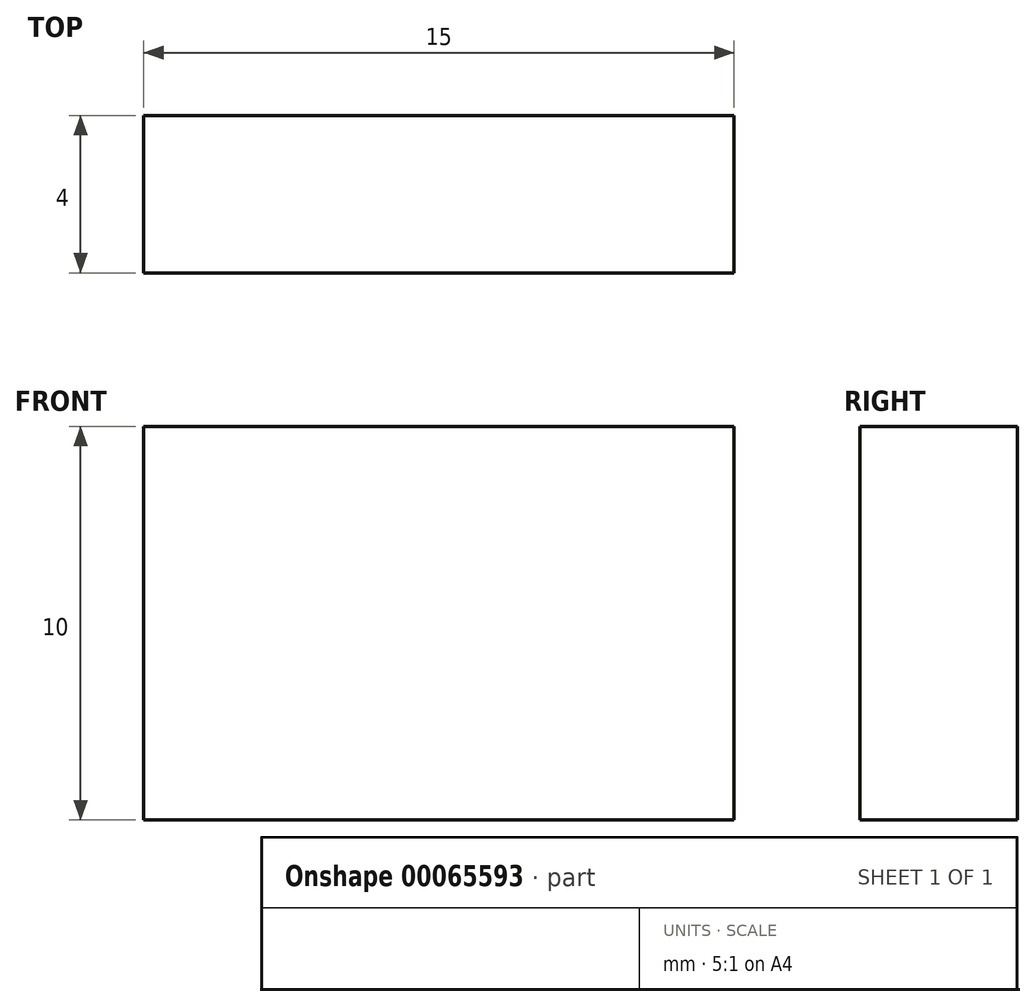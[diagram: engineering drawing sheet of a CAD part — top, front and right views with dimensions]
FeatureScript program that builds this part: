
annotation { "Feature Type Name" : "Feature", "Feature Type Description" : "" }
export const myFeature = defineFeature(function(context is Context, id is Id, definition is map)
    precondition{}
    {
        {
            var Q0;
            Q0=qCreatedBy(makeId("Front.planeOp"),FACE);
            var sketch = newSketch(context, id + "F0", { "sketchPlane" : qUnion([Q0])});
            skLineSegment(sketch, "E0", {"start": v(0, 10) * mm, "end": v(0, 0) * mm});
            skLineSegment(sketch, "E1", {"start": v(0, 0) * mm, "end": v(15, 0) * mm});
            skLineSegment(sketch, "E2", {"start": v(15, 0) * mm, "end": v(15, 10) * mm});
            skLineSegment(sketch, "E3", {"start": v(15, 10) * mm, "end": v(0, 10) * mm});
            skSolve(sketch);
        }
        {
            var Q0;
            Q0 = qSketchRegion(id + "F0", true);
            var Q1;
            Q1=makeQuery(id+"F0.imprint","IMPRINT",FACE,{"disambiguationData":[TD([[makeQuery(id+"F0.imprint","IMPRINT",EDGE,{"derivedFrom":sQuery(id+"F0.wireOp",EDGE,"E0")}),1.0]])]});
            extrude(context, id + "F1", {"entities" : qUnion([Q0, Q1]), "depth" : 4 * mm});
        }
    });
